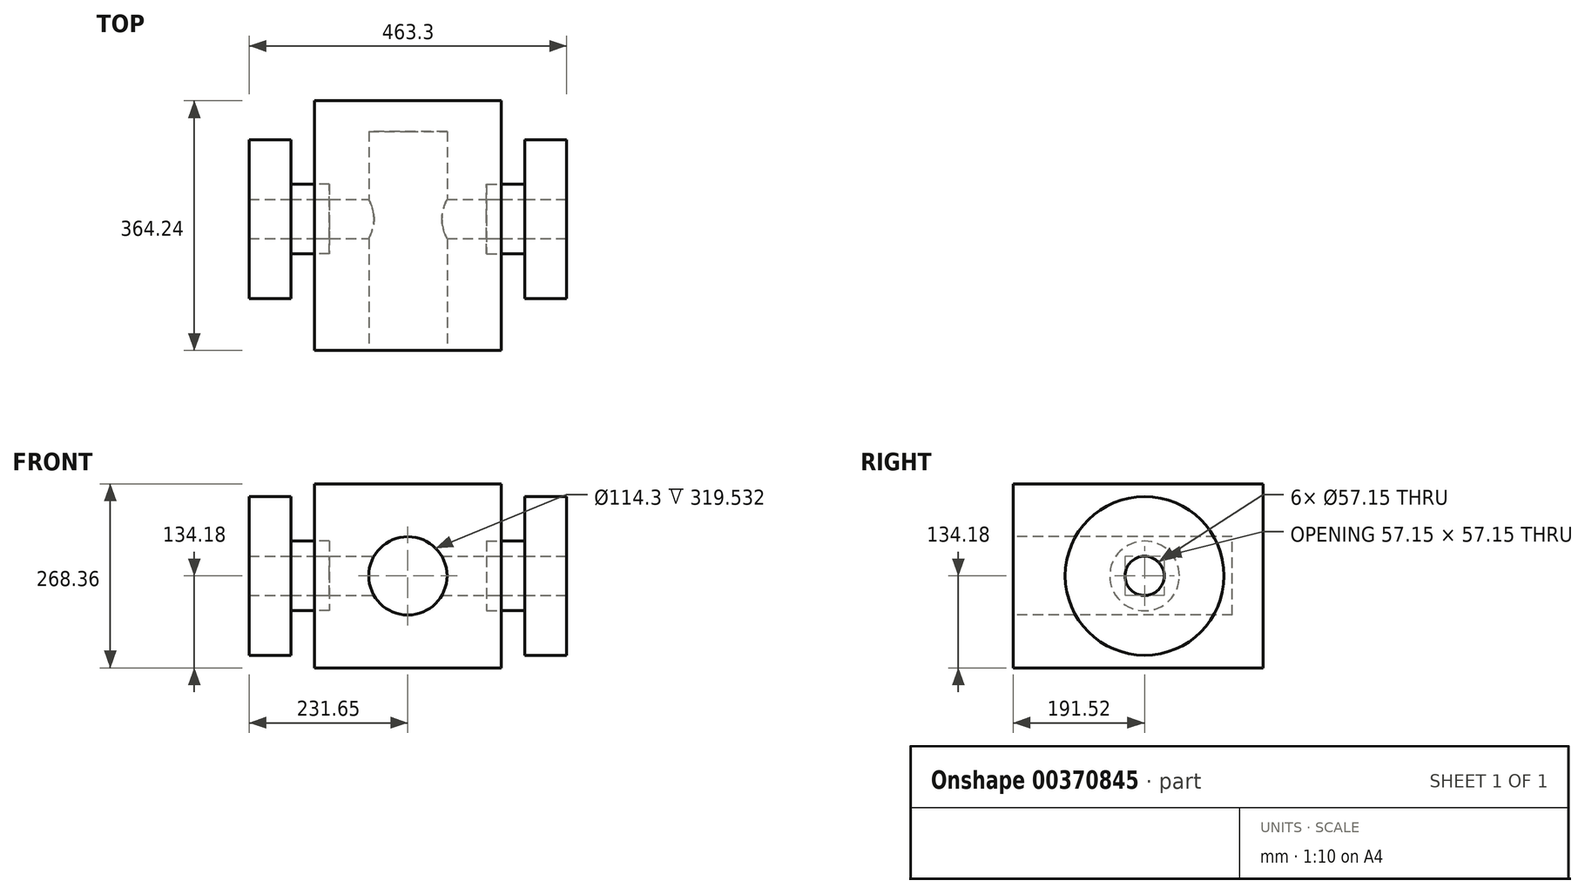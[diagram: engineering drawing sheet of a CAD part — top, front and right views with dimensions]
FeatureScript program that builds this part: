
annotation { "Feature Type Name" : "Feature", "Feature Type Description" : "" }
export const myFeature = defineFeature(function(context is Context, id is Id, definition is map)
    precondition{}
    {
        {
            var Q0;
            Q0=qCreatedBy(makeId("Front.planeOp"),FACE);
            var sketch = newSketch(context, id + "F0", { "sketchPlane" : qUnion([Q0])});
            skLineSegment(sketch, "E0.bottom", {"start": v(-136.4, -134.18) * mm, "end": v(136.4, -134.18) * mm});
            skLineSegment(sketch, "E0.top", {"start": v(-136.4, 134.18) * mm, "end": v(136.4, 134.18) * mm});
            skLineSegment(sketch, "E0.left", {"start": v(-136.4, -134.18) * mm, "end": v(-136.4, 134.18) * mm});
            skLineSegment(sketch, "E0.right", {"start": v(136.4, -134.18) * mm, "end": v(136.4, 134.18) * mm});
            skPoint(sketch, "E0.middle", {"position": v(0, 0) * mm});
            skSolve(sketch);
        }
        {
            var Q0;
            Q0 = qSketchRegion(id + "F0", true);
            extrude(context, id + "F1", {"entities" : qUnion([Q0]), "depth" : 191.52 * mm});
        }
        {
            var Q0;
            Q0=makeQuery(id+"F1.opExtrude","CAP_FACE",FACE,{"disambiguationData":[OSD([sQuery(id+"F0.wireOp",EDGE,"E0.bottom"),sQuery(id+"F0.wireOp",EDGE,"E0.top"),sQuery(id+"F0.wireOp",EDGE,"E0.left"),sQuery(id+"F0.wireOp",EDGE,"E0.right")])],"isStart":true});
            extrude(context, id + "F2", {"entities" : qUnion([Q0]), "operationType" : NewBodyOperationType.ADD, "depth" : 172.72 * mm});
        }
        {
            var Q0;
            Q0=qCreatedBy(makeId("Right.planeOp"),FACE);
            cPlane(context, id + "F3", {"entities" : qUnion([Q0]), "cplaneType" : CPlaneType.OFFSET, "offset" : 231.65 * mm, "width" : 152.4 * mm, "height" : 152.4 * mm});
        }
        {
            var Q0;
            Q0=qCreatedBy(id+"F3.planeOp",FACE);
            var sketch = newSketch(context, id + "F4", { "sketchPlane" : qUnion([Q0])});
            skCircle(sketch, "E1", {"center": v(0, 0) * mm, "radius": 115.82 * mm});
            skSolve(sketch);
        }
        {
            var Q0;
            Q0=makeQuery(id+"F4.imprint","IMPRINT",FACE,{"disambiguationData":[TD([[makeQuery(id+"F4.imprint","IMPRINT",EDGE,{"derivedFrom":sQuery(id+"F4.wireOp",EDGE,"E1")}),1.0]])]});
            var Q1;
            Q1 = qConstructionFilter(qBodyType(qCreatedBy(id + "F4" ,EDGE), BodyType.WIRE), ConstructionObject.NO);
            extrude(context, id + "F5", {"entities" : qUnion([Q0]), "surfaceEntities" : qUnion([Q1]), "oppositeDirection" : true, "depth" : 61.2 * mm});
        }
        {
            var Q0;
            Q0=makeQuery(id+"F5.opExtrude","CAP_FACE",FACE,{"disambiguationData":[OSD([sQuery(id+"F4.wireOp",EDGE,"E1")])],"isStart":false});
            var sketch = newSketch(context, id + "F6", { "sketchPlane" : qUnion([Q0])});
            skCircle(sketch, "E2", {"center": v(0, 0) * mm, "radius": 50.8 * mm});
            skSolve(sketch);
        }
        {
            var Q0;
            Q0 = qSketchRegion(id + "F6", true);
            extrude(context, id + "F7", {"entities" : qUnion([Q0]), "depth" : 55.88 * mm});
        }
        {
            var Q0;
            Q0=qCreatedBy(makeId("Right.planeOp"),FACE);
            var sketch = newSketch(context, id + "F8", { "sketchPlane" : qUnion([Q0])});
            skLineSegment(sketch, "E3", {"start": v(0, 0) * mm, "end": v(0, 210.58) * mm});
            skSolve(sketch);
        }
        {
            var Q0;
            Q0=makeQuery(id+"F7.opExtrude","SWEPT_BODY",BODY,{"disambiguationData":[OSD([sQuery(id+"F6.wireOp",EDGE,"E2")])]});
            var Q1;
            Q1=makeQuery(id+"F5.opExtrude","SWEPT_BODY",BODY,{"disambiguationData":[OSD([sQuery(id+"F4.wireOp",EDGE,"E1")])]});
            var Q2;
            Q2=sQuery(id+"F8.wireOp",EDGE,"E3");
            circularPattern(context, id + "F9", {"entities" : qUnion([Q0, Q1]), "axis" : qUnion([Q2]), "angle" : 360 * degree, "instanceCount" : 2, "equalSpace" : true});
        }
        {
            var Q0;
            Q0=makeQuery(id+"F5.opExtrude","CAP_FACE",FACE,{"disambiguationData":[OSD([sQuery(id+"F4.wireOp",EDGE,"E1")])],"isStart":true});
            var sketch = newSketch(context, id + "F10", { "sketchPlane" : qUnion([Q0])});
            skCircle(sketch, "E4", {"center": v(0, 0) * mm, "radius": 28.57 * mm});
            skSolve(sketch);
        }
        {
            var Q0;
            Q0 = qSketchRegion(id + "F10", true);
            extrude(context, id + "F11", {"entities" : qUnion([Q0]), "operationType" : NewBodyOperationType.REMOVE, "oppositeDirection" : true, "depth" : 701.04 * mm});
        }
        {
            var Q0;
            Q0=makeQuery(id+"F1.opExtrude","CAP_FACE",FACE,{"disambiguationData":[OSD([sQuery(id+"F0.wireOp",EDGE,"E0.bottom"),sQuery(id+"F0.wireOp",EDGE,"E0.top"),sQuery(id+"F0.wireOp",EDGE,"E0.left"),sQuery(id+"F0.wireOp",EDGE,"E0.right")])],"isStart":false});
            var sketch = newSketch(context, id + "F12", { "sketchPlane" : qUnion([Q0])});
            skCircle(sketch, "E5", {"center": v(0, 0) * mm, "radius": 57.15 * mm});
            skSolve(sketch);
        }
        {
            var Q0;
            Q0 = qSketchRegion(id + "F12", true);
            extrude(context, id + "F13", {"entities" : qUnion([Q0]), "operationType" : NewBodyOperationType.REMOVE, "oppositeDirection" : true, "depth" : 319.53 * mm});
        }
    });
